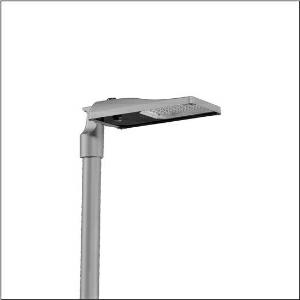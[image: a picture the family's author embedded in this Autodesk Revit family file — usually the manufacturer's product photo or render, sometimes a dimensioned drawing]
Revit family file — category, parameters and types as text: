
# Revit family: streetlight_sl_31_mini___p1_0a_5xh6a31t08ha_087d
name_source: partatom
category: Lighting Fixtures
units: mm (PartAtom-declared; Revit-internal decimal feet)

## family parameters
Cut with Voids When Loaded = No
Host = Face
Light Source = No
Part Type = Normal
Room Calculation Point = No
Round Connector Dimension = Use Diameter
Shared = No

## types (1)
- --- (1 x LED, 8970 lm, 68.3 W, 3000K)
    Apparent Load = 68 VA
    CIE Flux Codes = 23 55 94 100 100
    Color Rendering = 70
    Color Temperature = 3000K
    Default Elevation = 1800 mm
    Description = Streetlight SL 31 mini D4i, Desk-Remote mast luminaire for post-top, side-entry; light control with lens of PMMA; light distribution: P1.0a, direct asymmetric distribution, for standard-compliant lighting for roads and squares; LED: luminous flux: 8.970lm, light colour: 730, colour temperature: 3000K; luminous efficacy: 131,3lm/W; control: pre-setting: logarithmic dimming characteristic, flexible luminous flux parameterisation, time-dependent luminous flux control, constant luminous flux control, power reduction, intelligent temperature release in ECG and LED module, overheat protection; luminaire housing, of diecast aluminium, SITECO metallic grey (DB 702S), corrosivity category C5 high according to DIN EN ISO 12944; cover of toughened safety glass, transparent, opened without tools; mast flange of diecast aluminium, SITECO metallic grey (DB 702S), spigot size: 76/60mm, mast flange included unmounted; with cable H07RN-F 2x 1.5mm², cable length: 8,5m, connection cable pre-assembled; mains connection: 220..240V, AC, 50/60Hz; power consumption (at start of service life): 68,3W / (at end of service life): 74,5W / (with reduced operation 50%): 29,5W; protection rating (complete): IP66; insulation class (complete): insulation class II (safety insulation); impact resistance: IK09; certification: CE, ENEC, ENEC+, VDE, UKCA, ZD4i; permissible operating ambient temperature for outdoor applications: -40..+50°C; packaging unit: 1 piece

Light Distribution: P1.0a
    Height = 76 mm
    Lamp = 1 x LED
    Lamp Light Flux = 8970 lm
    Lamp Power = 68.3 W
    Lamp count = 1
    Length = 547 mm
    Luminous efficacy = 131 lm/W
    Manufacturer = Siteco
    ModVariant = No
    Model = 5XH6A31T08HA
    Number of Poles = 1
    OnlyDefault = Yes
    Power Factor = 1
    Product Name = Streetlight SL 31 mini | P1.0a
    Product group = mast luminaire | pylon top
    ProductGroupID = 6100
    Protection Class = Protection class II
    Protection Degree = IP 66
    RLX_Detail_Level = 1
    RLX_Emergency_Light_Flux = 0 lm
    RLX_Emergency_Type = 0
    RLX_Emergency_Type_DB = No
    RlxData = <blob elided: 24045 chars, md5=5b0dcc78>
    Socket = socket
    Standby Power = 0 W
    System Light Flux = 8970 lm
    System Power = 68 W
    Type Comments = factory setting: luminous flux: 100 % | dim-lin: 254 | 692 mA
    Type Image = l_1300332.jpg
    URL = http://relux.com
    VarID = @adj_027413
    Voltage = 0 V
    Weight = 0.00 kg
    Width = 265 mm

## geometry (parser evidence)
native form markers: Blend x4, Sweep x10
no freeform markers — native parametric forms only
